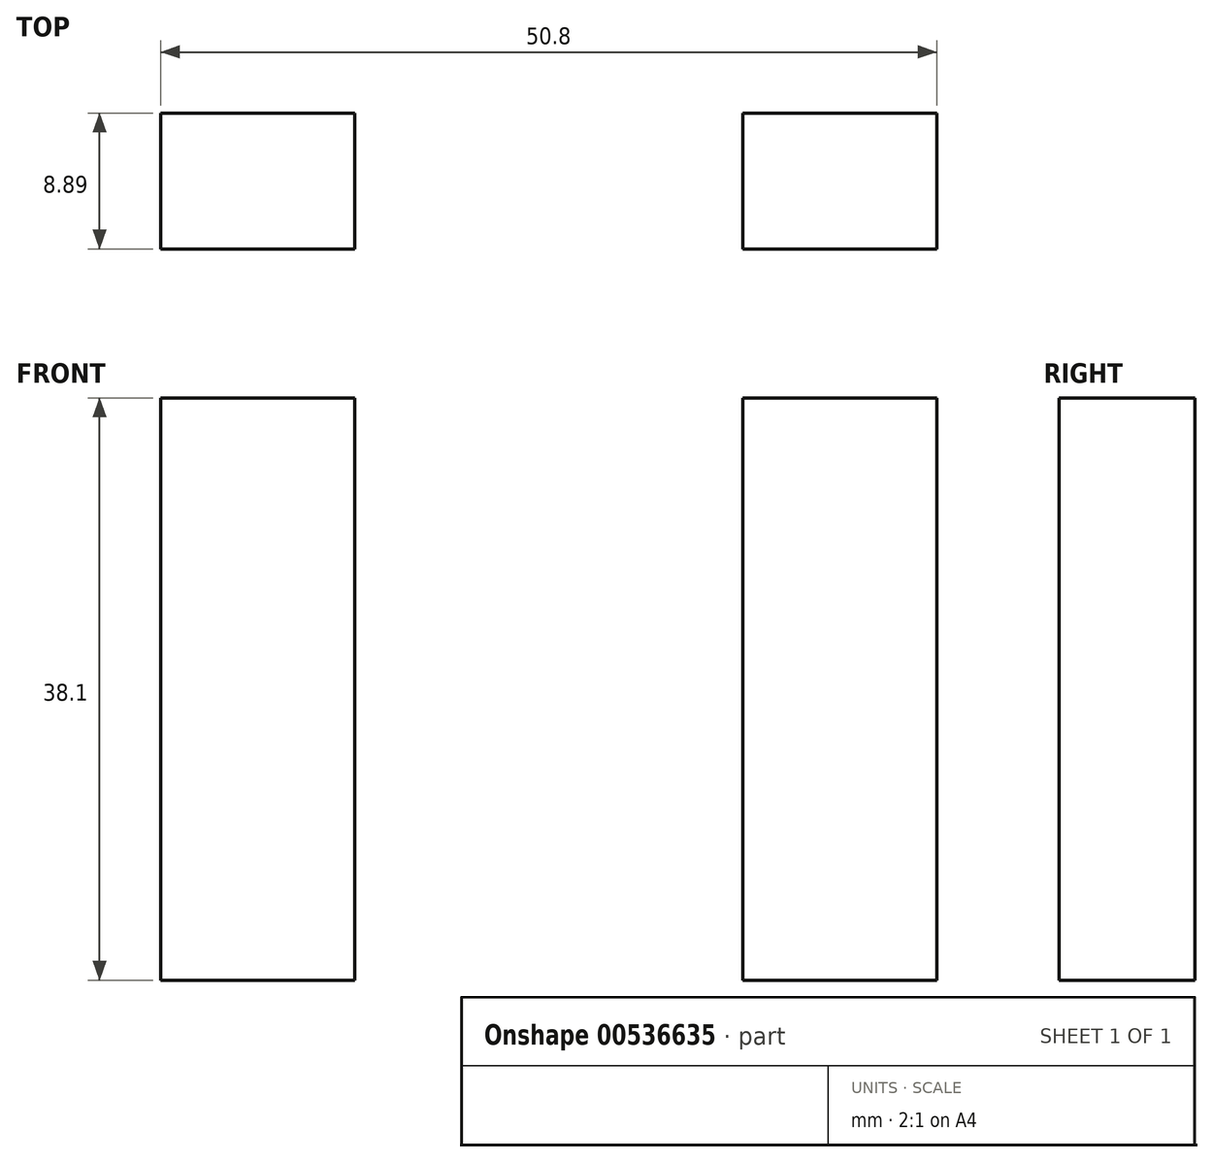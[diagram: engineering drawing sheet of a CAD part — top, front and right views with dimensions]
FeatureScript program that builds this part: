
annotation { "Feature Type Name" : "Feature", "Feature Type Description" : "" }
export const myFeature = defineFeature(function(context is Context, id is Id, definition is map)
    precondition{}
    {
        {
            var Q0;
            Q0=qCreatedBy(makeId("Front.planeOp"),FACE);
            var sketch = newSketch(context, id + "F0", { "sketchPlane" : qUnion([Q0])});
            skLineSegment(sketch, "E0", {"start": v(-52.67, 20.9) * mm, "end": v(-52.67, -17.2) * mm});
            skLineSegment(sketch, "E1", {"start": v(-52.67, -17.2) * mm, "end": v(-39.97, -17.2) * mm});
            skLineSegment(sketch, "E2", {"start": v(-52.67, 20.9) * mm, "end": v(-39.97, 20.9) * mm});
            skLineSegment(sketch, "E3", {"start": v(-39.97, 20.9) * mm, "end": v(-39.97, -17.2) * mm});
            skLineSegment(sketch, "E4", {"start": v(-27.27, 50.38) * mm, "end": v(-27.27, -21.85) * mm});
            skLineSegment(sketch, "E5.MirrorCS", {"start": v(-1.87, 20.9) * mm, "end": v(-14.57, 20.9) * mm});
            skLineSegment(sketch, "E6.MirrorCS", {"start": v(-14.57, 20.9) * mm, "end": v(-14.57, -17.2) * mm});
            skLineSegment(sketch, "E7.MirrorCS", {"start": v(-1.87, 20.9) * mm, "end": v(-1.87, -17.2) * mm});
            skLineSegment(sketch, "E8.MirrorCS", {"start": v(-1.87, -17.2) * mm, "end": v(-14.57, -17.2) * mm});
            skSolve(sketch);
        }
        {
            var Q0;
            Q0 = qSketchRegion(id + "F0", true);
            extrude(context, id + "F1", {"entities" : qUnion([Q0]), "depth" : 8.9 * mm, "offsetDistance" : 25.4 * mm});
        }
    });
